# Revit family: 1STERN_FAUCET_TOUCHLESS_SMART_PLUS
name_source: partatom
category: Generic Models
revit_build: Autodesk Revit 2017 (Build: 20160225_1515(x64)
units: mm (PartAtom-declared; Revit-internal decimal feet)

## family parameters
Can host rebar = No
Cut with Voids When Loaded = No
Host = Face
Part Type = Normal
Room Calculation Point = Yes
Round Connector Dimension = Use Diameter
Shared = No

## types (2) — shared parameters
AVAILABLE FINISHES = Brushed Nickel - Matt Black - Satin Gold - PVD Antique Bronze - PVD rose Gold - PVD Copper - AISI316 Material
BADGE = https://bim.archiproducts.com
DEPTH = 115 mm
Default Elevation = 1219 mm
Description = SMART - Touch-free electronic faucet for deck mounted installations.‎ Activated by infrared sensor.‎ Tall version for counter top washbasins.‎ For cold or premixed water.‎ Filters included.‎ Chrome plated body, other finishes available.‎ Latching solenoid valve is located above deck inside the product for added vandal protection.‎ Regular faucet installation with simple battery connection.‎ Adjustable settings by remote control: sensor range, security time, delay in, delay out, on-off and reset to factory settings.‎ 24 hour mandatory hygiene flush available upon request.‎
FINISHING MATERIAL = Chrome - Stern
HEIGHT = 338 mm  [stored 1.10892 ft]
INSTALLATION = Deck mounted
MATERIAL DESCRIPTION = Finish: Chrome
Manufacturer = Stern Engineering
OPERATING PRESSURE = 0.5 - 8.0 BAR (7- 116  PSI)
OPTIONS = Remote control (code 07100005), Matching battery-powered soap dispenser (code 235940), Matching transformer-powered soap dispenser combination (code 235930), Lead free versions (upon request)
PRODUCT SHEET = https://www.archiproducts.com
SECURITY TIME = Auto shutoff after 90 seconds. Adjustableby remote control.
TECHNICAL SHEET = https://www.sternfaucets.com
URL = http://www.sternfaucets.com
VOLTAGE = 9 V
WATER FLOW = 6.0 LPM
WATER SAVING OPTIONS = 4 LPM/1 GPM, 3 LPM/0.8 GPM, 1.89 LPM/0.5 GPM, 1.3 LPM/0.35 GPM - PCA spray
WATER SUPPLY = Cold or premixed water
WATER TEMPERATURE = 70°C Maximum
WIDTH = 50 mm  [stored 0.164042 ft]

## per-type parameters (varying)
| type | Model | POWER SUPPLY | PRODUCT CODE |
| SMART_PLUS - 9V BATTERY | Smart Plus B | 9V Battery | 235150 |
| SMART_PLUS - 9V TRANSFORMER | Smart Plus E | 9V Transformer | 235250 |

note: [stored X ft] marks values corroborated as IEEE doubles in the binary element streams (Revit-internal decimal feet)

## geometry (parser evidence)
native form markers: Blend x4, Sweep x2
no freeform markers — native parametric forms only
